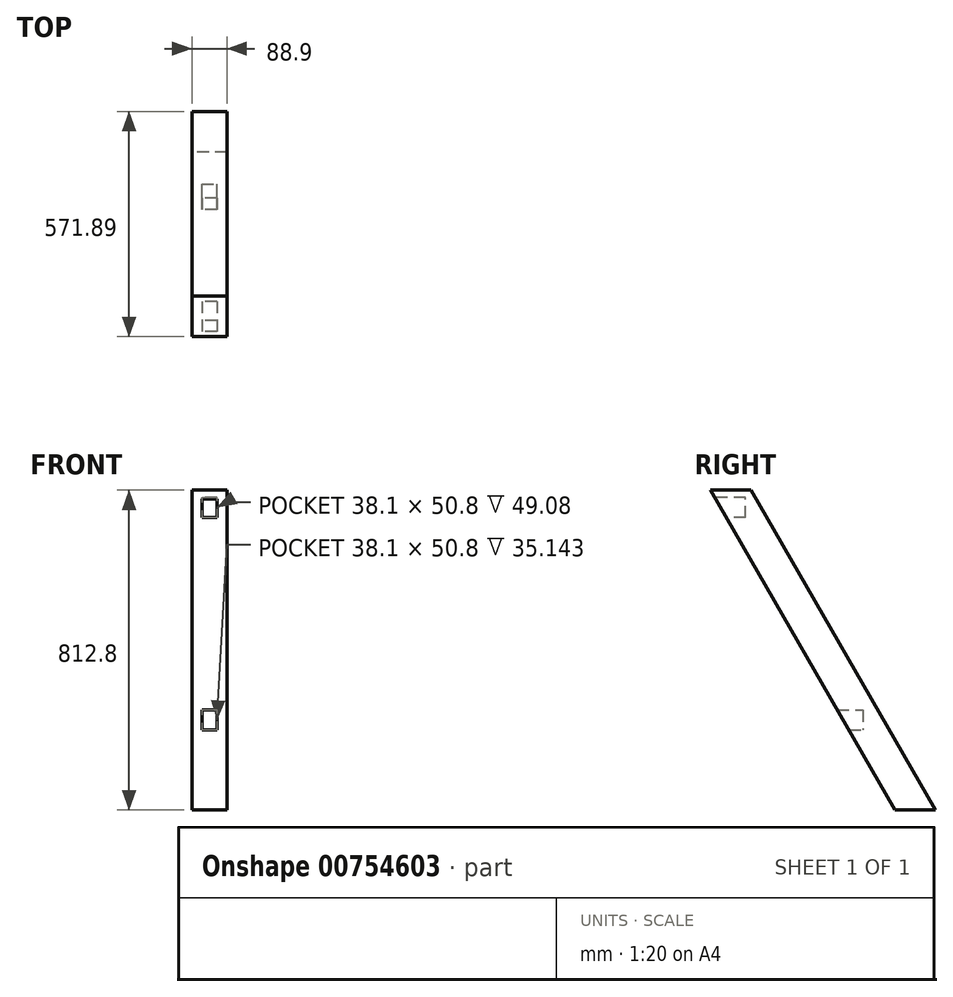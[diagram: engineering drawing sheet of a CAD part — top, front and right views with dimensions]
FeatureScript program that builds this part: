
annotation { "Feature Type Name" : "Feature", "Feature Type Description" : "" }
export const myFeature = defineFeature(function(context is Context, id is Id, definition is map)
    precondition{}
    {
        {
            var Q0;
            Q0=qCreatedBy(makeId("Right.planeOp"),FACE);
            var sketch = newSketch(context, id + "F0", { "sketchPlane" : qUnion([Q0])});
            skLineSegment(sketch, "E0", {"start": v(-285.5, 406.4) * mm, "end": v(-182.88, 406.4) * mm});
            skLineSegment(sketch, "E1", {"start": v(-182.88, 406.4) * mm, "end": v(286.4, -406.4) * mm});
            skLineSegment(sketch, "E2", {"start": v(286.4, -406.4) * mm, "end": v(183.77, -406.4) * mm});
            skLineSegment(sketch, "E3", {"start": v(183.77, -406.4) * mm, "end": v(-285.5, 406.4) * mm});
            skLineSegment(sketch, "E4", {"start": v(0, 406.4) * mm, "end": v(0, -406.4) * mm, "construction": true});
            skSolve(sketch);
        }
        {
            var Q0;
            Q0 = qSketchRegion(id + "F0", true);
            extrude(context, id + "F1", {"entities" : qUnion([Q0]), "endBound" : BoundingType.SYMMETRIC, "depth" : 88.9 * mm, "offsetDistance" : 25.4 * mm});
        }
        {
            var Q0;
            Q0=qCreatedBy(makeId("Front.planeOp"),FACE);
            cPlane(context, id + "F2", {"entities" : qUnion([Q0]), "cplaneType" : CPlaneType.OFFSET, "offset" : 272.3 * mm, "width" : 152.4 * mm, "height" : 152.4 * mm});
        }
        {
            var Q0;
            Q0=qCreatedBy(id+"F2.planeOp",FACE);
            var sketch = newSketch(context, id + "F3", { "sketchPlane" : qUnion([Q0])});
            skLineSegment(sketch, "E5", {"start": v(0, 406.4) * mm, "end": v(0, -406.4) * mm, "construction": true});
            skLineSegment(sketch, "E6.bottom", {"start": v(19.05, 336.55) * mm, "end": v(-19.05, 336.55) * mm});
            skLineSegment(sketch, "E6.top", {"start": v(19.05, 387.35) * mm, "end": v(-19.05, 387.35) * mm});
            skLineSegment(sketch, "E6.left", {"start": v(19.05, 336.55) * mm, "end": v(19.05, 387.35) * mm});
            skLineSegment(sketch, "E6.right", {"start": v(-19.05, 336.55) * mm, "end": v(-19.05, 387.35) * mm});
            skPoint(sketch, "E6.middle", {"position": v(0, 361.95) * mm});
            skSolve(sketch);
        }
        {
            var Q0;
            Q0 = qSketchRegion(id + "F3", true);
            extrude(context, id + "F4", {"entities" : qUnion([Q0]), "operationType" : NewBodyOperationType.REMOVE, "oppositeDirection" : true, "depth" : 76.2 * mm, "offsetDistance" : 25.4 * mm});
        }
        {
            var Q0;
            Q0=qCreatedBy(makeId("Front.planeOp"),FACE);
            cPlane(context, id + "F5", {"entities" : qUnion([Q0]), "cplaneType" : CPlaneType.OFFSET, "offset" : 101.6 * mm, "oppositeDirection" : true, "width" : 152.4 * mm, "height" : 152.4 * mm});
        }
        {
            var Q0;
            Q0=qCreatedBy(id+"F5.planeOp",FACE);
            var sketch = newSketch(context, id + "F6", { "sketchPlane" : qUnion([Q0])});
            skLineSegment(sketch, "E7", {"start": v(0, 406.4) * mm, "end": v(0, -406.4) * mm, "construction": true});
            skLineSegment(sketch, "E8.bottom", {"start": v(-19.05, -152.4) * mm, "end": v(19.05, -152.4) * mm});
            skLineSegment(sketch, "E8.top", {"start": v(-19.05, -203.2) * mm, "end": v(19.05, -203.2) * mm});
            skLineSegment(sketch, "E8.left", {"start": v(-19.05, -152.4) * mm, "end": v(-19.05, -203.2) * mm});
            skLineSegment(sketch, "E8.right", {"start": v(19.05, -152.4) * mm, "end": v(19.05, -203.2) * mm});
            skPoint(sketch, "E8.middle", {"position": v(0, -177.8) * mm});
            skSolve(sketch);
        }
        {
            var Q0;
            Q0 = qSketchRegion(id + "F6", true);
            extrude(context, id + "F7", {"entities" : qUnion([Q0]), "operationType" : NewBodyOperationType.REMOVE, "depth" : 76.2 * mm, "offsetDistance" : 25.4 * mm});
        }
    });
